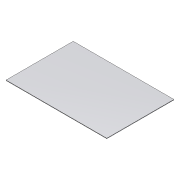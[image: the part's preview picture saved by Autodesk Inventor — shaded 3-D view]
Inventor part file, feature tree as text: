
AUTODESK INVENTOR PART (.ipt)
format: ipt  version: 2012 (Build 160160000, 160)  size: 69,632 bytes
history: native  units: in
note: dims shown in document units (in); Inventor stores cm internally (conversion verified against a paired STEP export)
features: extrude x1, sketch x1
ambient origin geometry x8: Origin, YZ Plane, XZ Plane, XY Plane, X Axis, Y Axis, Z Axis, Center Point
feature tree (2):
  extrude  "Extrusion2"  TaperAngle=0.0deg  [1 undecoded]
  sketch  "Sketch2"  dims[d6=27.0in d7=0.0in d8=18.0in d9=0.125in d10=0.0in d12=9.0in]
note: 1 required parameter value undecoded (feature->parameter linkage not recoverable at this tier; creation-order binding heuristic only, values carry confidence <= 0.55)
